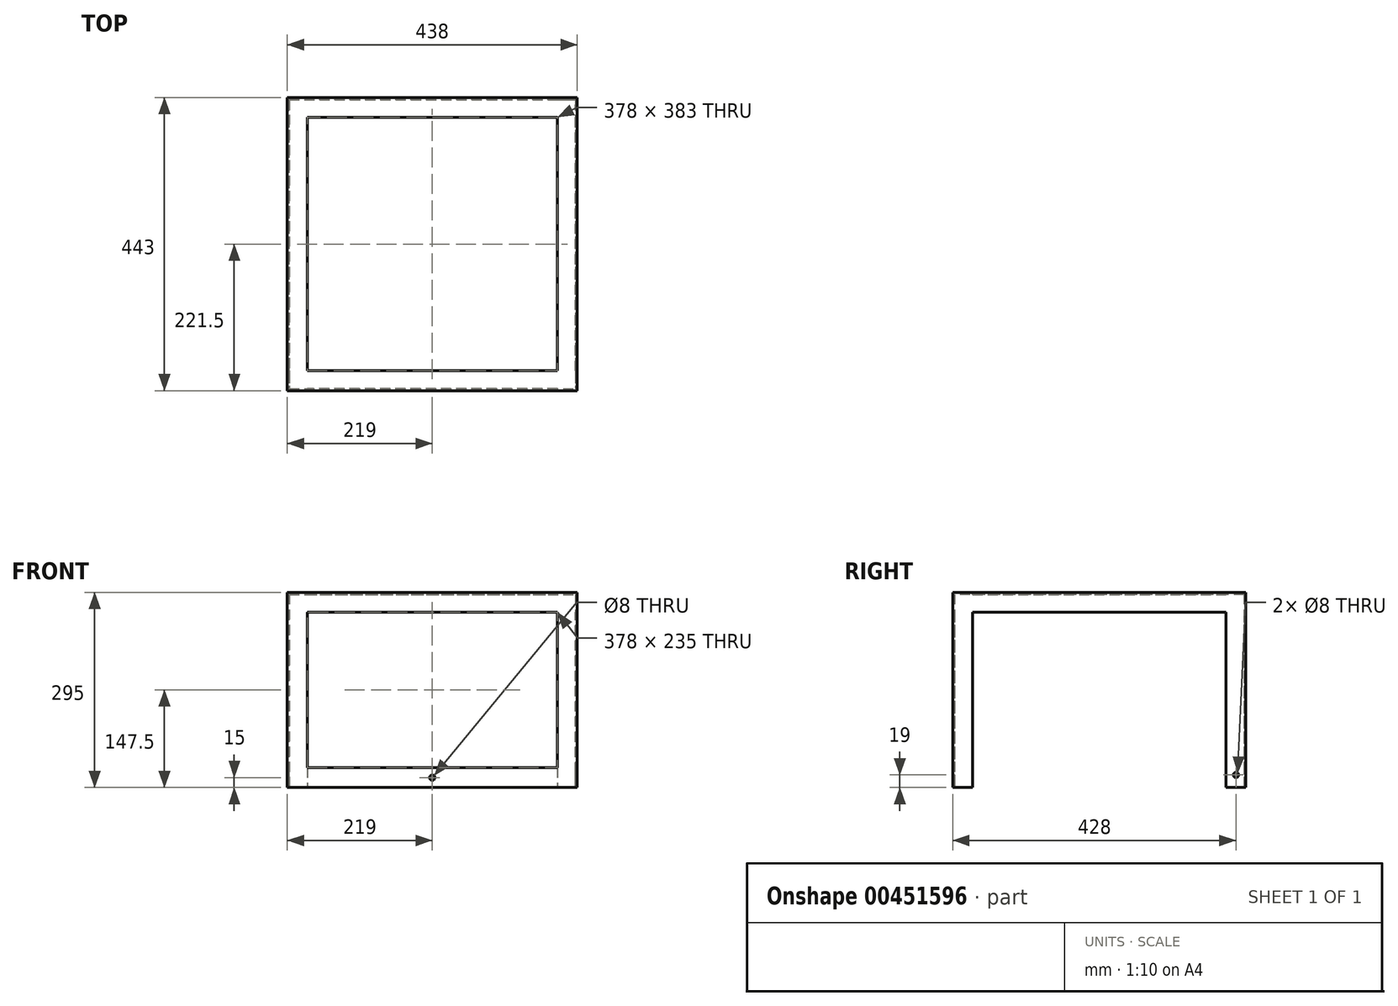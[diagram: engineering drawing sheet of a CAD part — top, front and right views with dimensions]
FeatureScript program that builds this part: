
annotation { "Feature Type Name" : "Feature", "Feature Type Description" : "" }
export const myFeature = defineFeature(function(context is Context, id is Id, definition is map)
    precondition{}
    {
        {
            var Q0;
            Q0=qCreatedBy(makeId("Top.planeOp"),FACE);
            var sketch = newSketch(context, id + "F0", { "sketchPlane" : qUnion([Q0])});
            skLineSegment(sketch, "E0.bottom", {"start": v(-219, 221.5) * mm, "end": v(219, 221.5) * mm});
            skLineSegment(sketch, "E0.top", {"start": v(-219, -221.5) * mm, "end": v(219, -221.5) * mm});
            skLineSegment(sketch, "E0.left", {"start": v(-219, 221.5) * mm, "end": v(-219, -221.5) * mm});
            skLineSegment(sketch, "E0.right", {"start": v(219, 221.5) * mm, "end": v(219, -221.5) * mm});
            skLineSegment(sketch, "E1", {"start": v(0, 221.5) * mm, "end": v(0, -221.5) * mm, "construction": true});
            skLineSegment(sketch, "E2", {"start": v(-219, 0) * mm, "end": v(219, 0) * mm, "construction": true});
            skSolve(sketch);
        }
        {
            var Q0;
            Q0 = qSketchRegion(id + "F0", true);
            extrude(context, id + "F1", {"entities" : qUnion([Q0]), "depth" : 295 * mm});
        }
        {
            var Q0;
            Q0=makeQuery(id+"F1.opExtrude","CAP_FACE",FACE,{"disambiguationData":[OSD([sQuery(id+"F0.wireOp",EDGE,"E0.bottom"),sQuery(id+"F0.wireOp",EDGE,"E0.top"),sQuery(id+"F0.wireOp",EDGE,"E0.left"),sQuery(id+"F0.wireOp",EDGE,"E0.right")])],"isStart":true});
            shell(context, id + "F2", {"entities" : qUnion([Q0]), "thickness" : 3 * mm});
        }
        {
            var Q0;
            Q0=qCreatedBy(makeId("Front.planeOp"),FACE);
            var sketch = newSketch(context, id + "F3", { "sketchPlane" : qUnion([Q0])});
            skLineSegment(sketch, "E3.bottom", {"start": v(-189, 0) * mm, "end": v(189, 0) * mm});
            skLineSegment(sketch, "E3.top", {"start": v(-189, 265) * mm, "end": v(189, 265) * mm});
            skLineSegment(sketch, "E3.left", {"start": v(-189, 0) * mm, "end": v(-189, 265) * mm});
            skLineSegment(sketch, "E3.right", {"start": v(189, 0) * mm, "end": v(189, 265) * mm});
            skLineSegment(sketch, "E4", {"start": v(0, 265) * mm, "end": v(0, 0) * mm, "construction": true});
            skSolve(sketch);
        }
        {
            var Q0;
            Q0 = qSketchRegion(id + "F3", true);
            extrude(context, id + "F4", {"entities" : qUnion([Q0]), "operationType" : NewBodyOperationType.REMOVE, "endBound" : BoundingType.THROUGH_ALL, "oppositeDirection" : true, "depth" : 25 * mm, "hasSecondDirection" : true, "secondDirectionBound" : SecondDirectionBoundingType.THROUGH_ALL, "secondDirectionOppositeDirection" : false, "secondDirectionDepth" : 25 * mm});
        }
        {
            var Q0;
            Q0=qCreatedBy(makeId("Right.planeOp"),FACE);
            var sketch = newSketch(context, id + "F5", { "sketchPlane" : qUnion([Q0])});
            skLineSegment(sketch, "E5.bottom", {"start": v(-191.5, 0) * mm, "end": v(191.5, 0) * mm});
            skLineSegment(sketch, "E5.top", {"start": v(-191.5, 265) * mm, "end": v(191.5, 265) * mm});
            skLineSegment(sketch, "E5.left", {"start": v(-191.5, 0) * mm, "end": v(-191.5, 265) * mm});
            skLineSegment(sketch, "E5.right", {"start": v(191.5, 0) * mm, "end": v(191.5, 265) * mm});
            skLineSegment(sketch, "E6", {"start": v(0, 265) * mm, "end": v(0, 0) * mm, "construction": true});
            skSolve(sketch);
        }
        {
            var Q0;
            Q0 = qSketchRegion(id + "F5", true);
            extrude(context, id + "F6", {"entities" : qUnion([Q0]), "operationType" : NewBodyOperationType.REMOVE, "endBound" : BoundingType.THROUGH_ALL, "oppositeDirection" : true, "depth" : 25 * mm, "hasSecondDirection" : true, "secondDirectionBound" : SecondDirectionBoundingType.THROUGH_ALL, "secondDirectionOppositeDirection" : false, "secondDirectionDepth" : 25 * mm});
        }
        {
            var Q0;
            Q0=makeQuery(id+"F1.opExtrude","CAP_FACE",FACE,{"disambiguationData":[OSD([sQuery(id+"F0.wireOp",EDGE,"E0.bottom"),sQuery(id+"F0.wireOp",EDGE,"E0.top"),sQuery(id+"F0.wireOp",EDGE,"E0.left"),sQuery(id+"F0.wireOp",EDGE,"E0.right")])],"isStart":false});
            var sketch = newSketch(context, id + "F7", { "sketchPlane" : qUnion([Q0])});
            skLineSegment(sketch, "E7.bottom", {"start": v(-189, -191.5) * mm, "end": v(189, -191.5) * mm});
            skLineSegment(sketch, "E7.top", {"start": v(-189, 191.5) * mm, "end": v(189, 191.5) * mm});
            skLineSegment(sketch, "E7.left", {"start": v(-189, -191.5) * mm, "end": v(-189, 191.5) * mm});
            skLineSegment(sketch, "E7.right", {"start": v(189, -191.5) * mm, "end": v(189, 191.5) * mm});
            skLineSegment(sketch, "E8", {"start": v(-189, 0) * mm, "end": v(189, 0) * mm, "construction": true});
            skLineSegment(sketch, "E9", {"start": v(0, 191.5) * mm, "end": v(0, -191.5) * mm, "construction": true});
            skSolve(sketch);
        }
        {
            var Q0;
            Q0 = qSketchRegion(id + "F7", true);
            extrude(context, id + "F8", {"entities" : qUnion([Q0]), "operationType" : NewBodyOperationType.REMOVE, "endBound" : BoundingType.THROUGH_ALL, "oppositeDirection" : true, "depth" : 25 * mm});
        }
        {
            var Q0;
            Q0=makeQuery(id+"F1.opExtrude","SWEPT_FACE",FACE,{"disambiguationData":[OSD([sQuery(id+"F0.wireOp",EDGE,"E0.top")])]});
            var sketch = newSketch(context, id + "F9", { "sketchPlane" : qUnion([Q0])});
            skLineSegment(sketch, "E10.bottom", {"start": v(-189, 0) * mm, "end": v(189, 0) * mm});
            skLineSegment(sketch, "E10.top", {"start": v(-189, 30) * mm, "end": v(189, 30) * mm});
            skLineSegment(sketch, "E10.left", {"start": v(-189, 0) * mm, "end": v(-189, 30) * mm});
            skLineSegment(sketch, "E10.right", {"start": v(189, 0) * mm, "end": v(189, 30) * mm});
            skCircle(sketch, "E11", {"center": v(0, 15) * mm, "radius": 4 * mm});
            skSolve(sketch);
        }
        {
            var Q0;
            Q0 = qSketchRegion(id + "F9", true);
            var Q1;
            Q1=makeQuery(id+"F2.opShell","OFFSET_FACE",FACE,{"disambiguationData":[OSD([sQuery(id+"F0.wireOp",EDGE,"E0.top")])]});
            extrude(context, id + "F10", {"entities" : qUnion([Q0]), "operationType" : NewBodyOperationType.ADD, "endBound" : BoundingType.UP_TO_SURFACE, "oppositeDirection" : true, "endBoundEntityFace" : qUnion([Q1]), "depth" : 25 * mm});
        }
        {
            var Q0;
            Q0=makeQuery(id+"F1.opExtrude","SWEPT_FACE",FACE,{"disambiguationData":[OSD([sQuery(id+"F0.wireOp",EDGE,"E0.right")])]});
            var sketch = newSketch(context, id + "F11", { "sketchPlane" : qUnion([Q0])});
            skCircle(sketch, "E12", {"center": v(206.5, 19) * mm, "radius": 4 * mm});
            skSolve(sketch);
        }
        {
            var Q0;
            Q0 = qSketchRegion(id + "F11", true);
            extrude(context, id + "F12", {"entities" : qUnion([Q0]), "operationType" : NewBodyOperationType.REMOVE, "endBound" : BoundingType.THROUGH_ALL, "oppositeDirection" : true, "depth" : 25 * mm});
        }
    });
